# Revit family: Haworth_MSeries_Storage_Locker_AP_PRELIMINARY
name_source: partatom
category: Furniture Systems
units: mm (PartAtom-declared; Revit-internal decimal feet)

## family parameters
Always vertical = Yes
Cut with Voids When Loaded = No
OmniClass Number = 23.40.70.14.64.21
OmniClass Title = Systems Furniture
Part Type = Normal
Room Calculation Point = No
Round Connector Dimension = Use Diameter
Shared = No
Work Plane-Based = No

## types (7) — shared parameters
Assembly Code = E2020200
Bottom Case Offset = 30 mm  [stored 0.0984252 ft]
Case Thickness = 20 mm  [stored 0.0656168 ft]
Description = Haworth - M Series - Storage - Locker
Distance Between Drawer = 2 mm  [stored 0.00656168 ft]
Glide Finish = Haworth _ Polymer _ Black
Lock Finish = Haworth _ Polymer _ Black
Manufacturer = Haworth
Max. Width = 900 mm  [stored 2.95276 ft]
Min. Width = 450 mm  [stored 1.47638 ft]
Model = STMSKXX
Pull Finish = Haworth _ Paint _ Smooth Plaster
Revision Number = 1
Size = Verify Final Dim. w/ Haworth
Trim Finish = Haworth _ Polymer _ Black
URL = https://www.haworth.com
URL - Product = https://www.haworth.com
Warranty = http://www.haworth.com

## per-type parameters (varying)
| type | Actual Depth | Actual Height | Actual Width | Drawer Height | Drawer Width | Freestanding | Hanging | Level Offset | Lock Offset Side | Lock Offset Top | Modular | Slim | Stack on | Three Drawer | Total Drawer Height | Two Drawer | Width | not Slim |
| Stack on | 500 mm  [stored 1.64042 ft] | 800 mm  [stored 2.62467 ft] | 900 mm  [stored 2.95276 ft] | 385 mm  [stored 1.26312 ft] | 446 mm | No | Yes | 400 mm  [stored 1.31234 ft] | 411 mm  [stored 1.34843 ft] | 50 mm  [stored 0.164042 ft] | No | No | Yes | No | 770 mm  [stored 2.52625 ft] | Yes | 900 mm  [stored 2.95276 ft] | Yes |
| Modular | 450 mm  [stored 1.47638 ft] | 845 mm  [stored 2.77231 ft] | 800 mm  [stored 2.62467 ft] | 408 mm | 396 mm | Yes | No | 0 mm  [stored 0 ft] | 361 mm  [stored 1.18438 ft] | 950 mm  [stored 3.1168 ft] | Yes | No | No | No | 815 mm  [stored 2.67388 ft] | Yes | 800 mm  [stored 2.62467 ft] | Yes |
| Freestanding 4Hi Small | 450 mm  [stored 1.47638 ft] | 845 mm  [stored 2.77231 ft] | 900 mm  [stored 2.95276 ft] | 408 mm | 446 mm | Yes | No | 0 mm  [stored 0 ft] | 411 mm  [stored 1.34843 ft] | 50 mm  [stored 0.164042 ft] | No | No | No | No | 815 mm  [stored 2.67388 ft] | Yes | 900 mm  [stored 2.95276 ft] | Yes |
| Freestanding 4Hi Tall | 450 mm  [stored 1.47638 ft] | 1140 mm  [stored 3.74016 ft] | 900 mm  [stored 2.95276 ft] | 555 mm | 446 mm | Yes | No | 0 mm  [stored 0 ft] | 411 mm  [stored 1.34843 ft] | 950 mm  [stored 3.1168 ft] | No | No | No | No | 1110 mm | Yes | 900 mm  [stored 2.95276 ft] | Yes |
| Freestanding 6Hi Small | 450 mm  [stored 1.47638 ft] | 1500 mm  [stored 4.92126 ft] | 900 mm  [stored 2.95276 ft] | 490 mm  [stored 1.60761 ft] | 446 mm | Yes | No | 0 mm  [stored 0 ft] | 411 mm  [stored 1.34843 ft] | 500 mm  [stored 1.64042 ft] | No | No | No | Yes | 1470 mm | No | 900 mm  [stored 2.95276 ft] | Yes |
| Freestanding 6Hi Tall | 500 mm  [stored 1.64042 ft] | 1800 mm  [stored 5.90551 ft] | 900 mm  [stored 2.95276 ft] | 590 mm | 446 mm | Yes | No | 0 mm  [stored 0 ft] | 411 mm  [stored 1.34843 ft] | 950 mm  [stored 3.1168 ft] | No | No | No | Yes | 1770 mm | No | 900 mm  [stored 2.95276 ft] | Yes |
| Freestanding 6Hi Slim | 500 mm  [stored 1.64042 ft] | 1800 mm  [stored 5.90551 ft] | 450 mm  [stored 1.47638 ft] | 885 mm | 221 mm  [stored 0.725066 ft] | Yes | No | 0 mm  [stored 0 ft] | 186 mm  [stored 0.610236 ft] | 950 mm  [stored 3.1168 ft] | No | Yes | No | No | 1770 mm | Yes | 450 mm  [stored 1.47638 ft] | No |

type visibility flags (boolean, named after types; folded from table):
- Stack on: Yes: (none)
- Modular: Yes: (none)
- Freestanding 4Hi Small: Yes: Freestanding 4Hi Small
- Freestanding 4Hi Tall: Yes: Freestanding 4Hi Tall
- Freestanding 6Hi Small: Yes: Freestanding 6Hi Small
- Freestanding 6Hi Tall: Yes: Freestanding 6Hi Tall
- Freestanding 6Hi Slim: Yes: Freestanding 6Hi Slim

note: [stored X ft] marks values corroborated as IEEE doubles in the binary element streams (Revit-internal decimal feet)

## geometry (parser evidence)
native form markers: Sweep x9
no freeform markers — native parametric forms only
